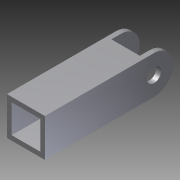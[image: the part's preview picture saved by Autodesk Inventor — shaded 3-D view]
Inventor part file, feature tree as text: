
AUTODESK INVENTOR PART (.ipt)
format: ipt  version: 2012 (Build 160160000, 160)  size: 119,808 bytes
history: native  units: in
note: dims shown in document units (in); Inventor stores cm internally (conversion verified against a paired STEP export)
features: extrude x3, sketch x3
ambient origin geometry x8: Origin, YZ Plane, XZ Plane, XY Plane, X Axis, Y Axis, Z Axis, Center Point
bodies: Solid1 (feature_tree)
feature tree (6):
  extrude  "Extrusion1"  Depth=1.0in
  extrude  "Extrusion2"  Depth=0.125in
  extrude  "Extrusion3"  Depth=0.125in
  sketch  "Sketch1"  dims[d0=1.0in d1=1.0in]
  sketch  "Sketch2"  dims[d2=0.125in d3=0.125in]
  sketch  "Sketch3"  dims[d4=0.125in d5=0.125in d6=3.375in d7=0.0in d8=0.375in d9=0.5in d10=0.5in d11=1.0in d12=0.0in d13=0.75in d14=0.125in d15=1.0in d16=0.0in d17=0.625in d18=0.25in]
